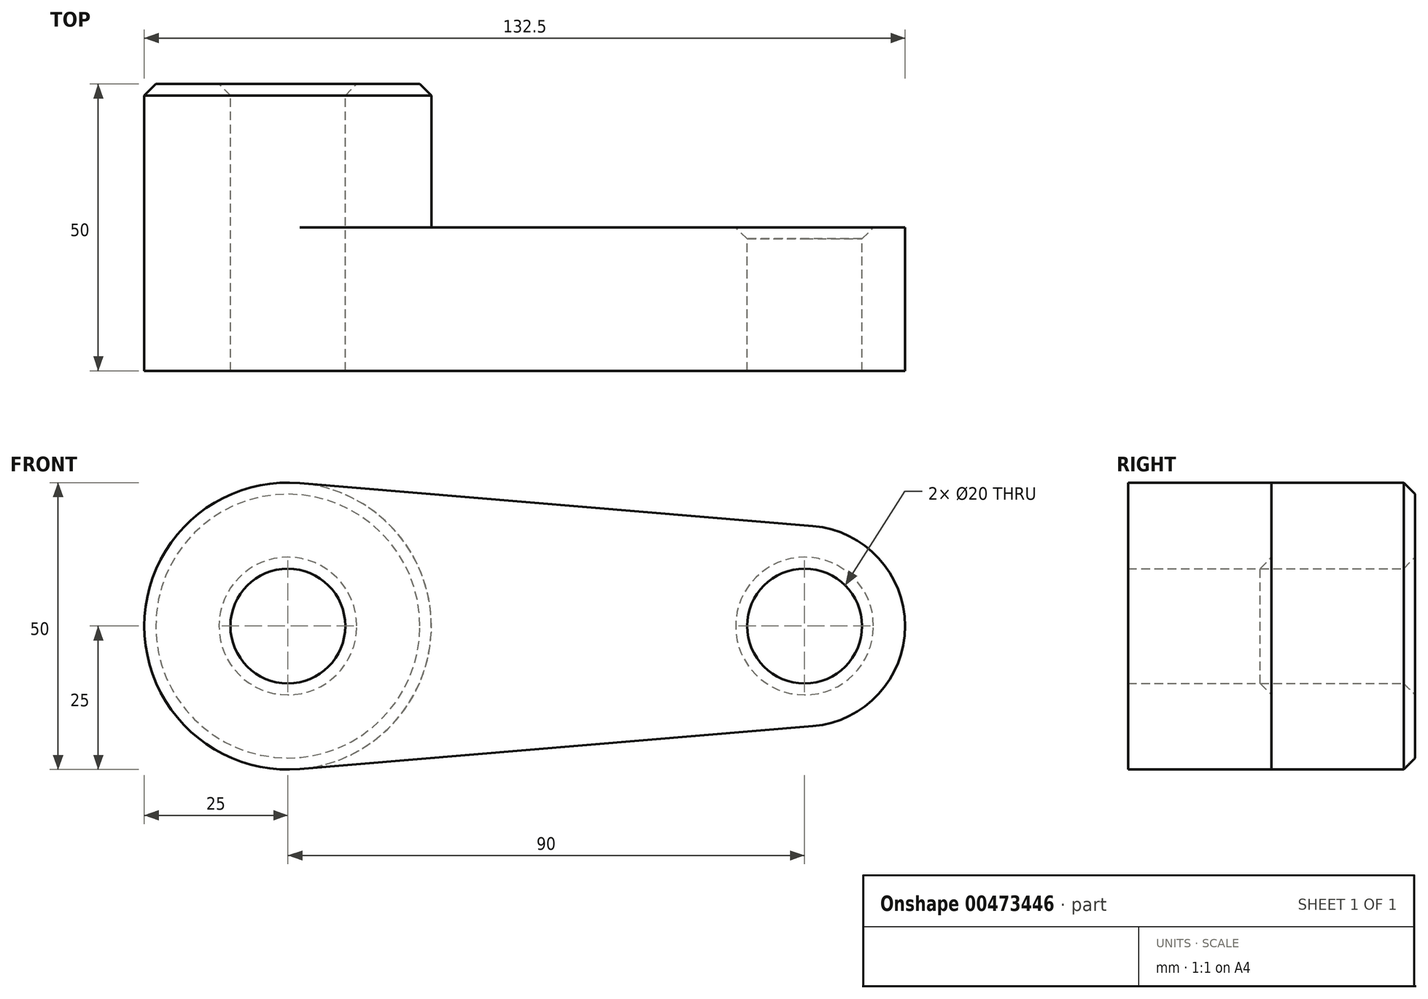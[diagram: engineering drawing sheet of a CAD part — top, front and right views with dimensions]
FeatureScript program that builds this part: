
annotation { "Feature Type Name" : "Feature", "Feature Type Description" : "" }
export const myFeature = defineFeature(function(context is Context, id is Id, definition is map)
    precondition{}
    {
        {
            var Q0;
            Q0=qCreatedBy(makeId("Front.planeOp"),FACE);
            var sketch = newSketch(context, id + "F0", { "sketchPlane" : qUnion([Q0])});
            skCircle(sketch, "E0", {"center": v(0, 0) * mm, "radius": 25 * mm});
            skCircle(sketch, "E1", {"center": v(90, 0) * mm, "radius": 17.5 * mm});
            skLineSegment(sketch, "E2", {"start": v(2.08, 24.91) * mm, "end": v(91.46, 17.44) * mm});
            skLineSegment(sketch, "E3", {"start": v(2.08, -24.91) * mm, "end": v(91.46, -17.44) * mm});
            skCircle(sketch, "E4", {"center": v(0, 0) * mm, "radius": 10 * mm});
            skCircle(sketch, "E5", {"center": v(90, 0) * mm, "radius": 10 * mm});
            skSolve(sketch);
        }
        {
            var Q0;
            Q0 = qSketchRegion(id + "F0", true);
            extrude(context, id + "F1", {"entities" : qUnion([Q0]), "depth" : 25 * mm});
        }
        {
            var Q0;
            Q0=makeQuery(id+"F0.imprint","IMPRINT",FACE,{"disambiguationData":[TD([[makeQuery(id+"F0.imprint","IMPRINT",EDGE,{"derivedFrom":sQuery(id+"F0.wireOp",EDGE,"E4")}),-1.0]])]});
            extrude(context, id + "F2", {"entities" : qUnion([Q0]), "operationType" : NewBodyOperationType.ADD, "depth" : 25 * mm, "hasSecondDirection" : true, "secondDirectionOppositeDirection" : true, "secondDirectionDepth" : 25 * mm});
        }
        {
            var Q0;
            Q0=makeQuery(id+"F1.opExtrude","CAP_EDGE",EDGE,{"disambiguationData":[OSD([sQuery(id+"F0.wireOp",EDGE,"E5")])],"isStart":true});
            var Q1;
            Q1=makeQuery(id+"F2.opExtrude","CAP_EDGE",EDGE,{"disambiguationData":[OSD([sQuery(id+"F0.wireOp",EDGE,"E0")])],"isStart":true});
            var Q2;
            Q2=makeQuery(id+"F2.opExtrude","CAP_EDGE",EDGE,{"disambiguationData":[OSD([sQuery(id+"F0.wireOp",EDGE,"E4")])],"isStart":true});
            chamfer(context, id + "F3", {"entities" : qUnion([Q0, Q1, Q2]), "width" : 2 * mm, "tangentPropagation" : true});
        }
    });
